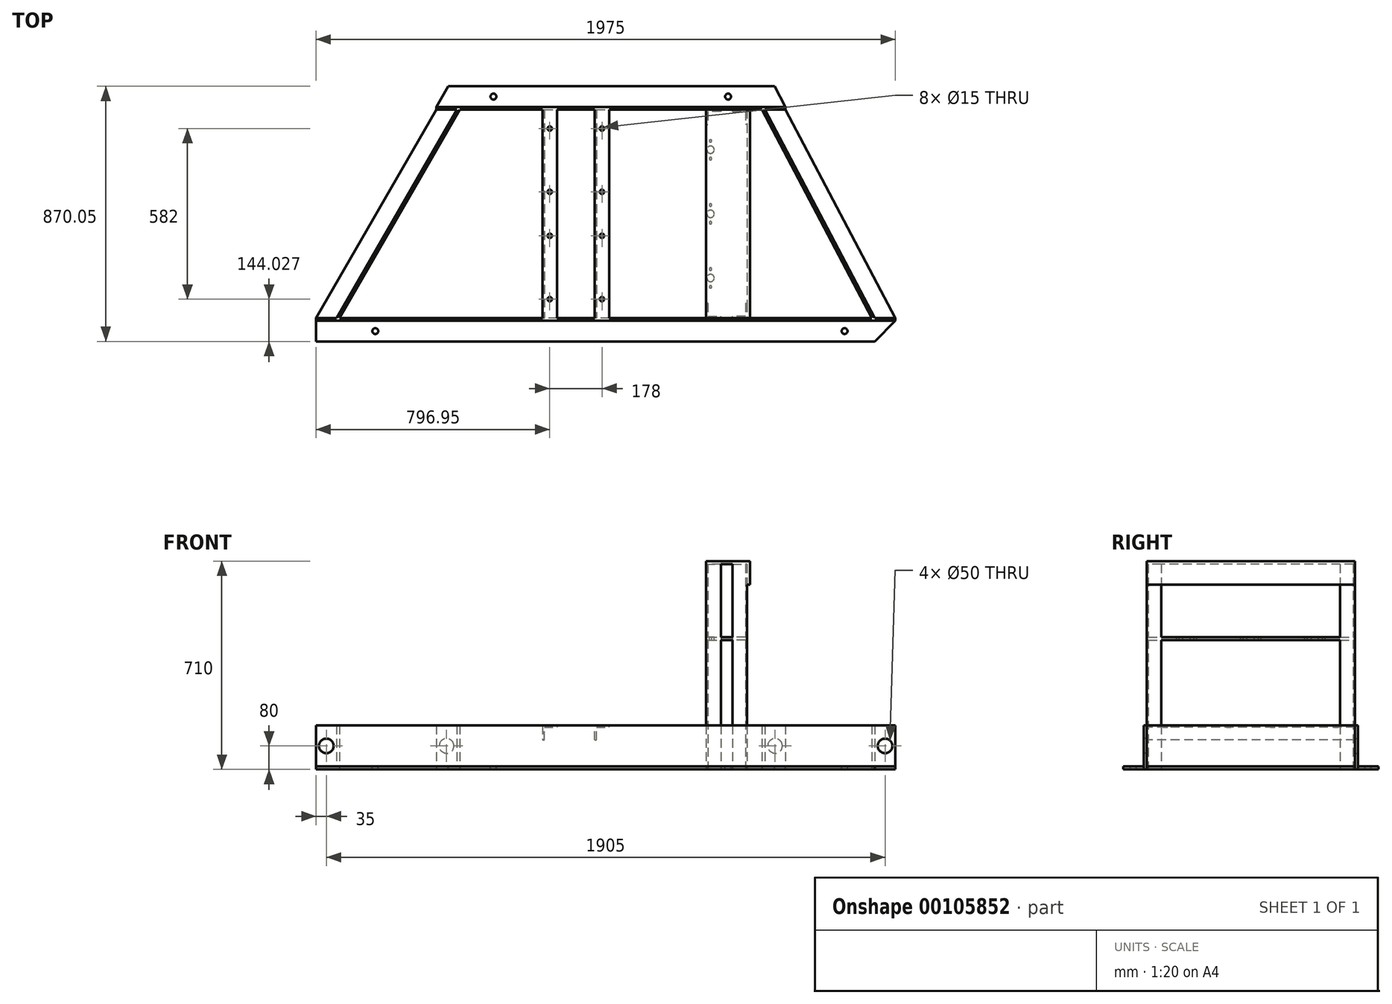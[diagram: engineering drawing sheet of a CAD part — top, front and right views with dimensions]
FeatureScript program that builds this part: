
annotation { "Feature Type Name" : "Feature", "Feature Type Description" : "" }
export const myFeature = defineFeature(function(context is Context, id is Id, definition is map)
    precondition{}
    {
        {
            var Q0;
            Q0=qCreatedBy(makeId("Right.planeOp"),FACE);
            var sketch = newSketch(context, id + "F0", { "sketchPlane" : qUnion([Q0])});
            skLineSegment(sketch, "E0.bottom", {"start": v(0, 0) * mm, "end": v(80, 0) * mm});
            skLineSegment(sketch, "E0.top", {"start": v(0, 10) * mm, "end": v(80, 10) * mm});
            skLineSegment(sketch, "E0.left", {"start": v(0, 0) * mm, "end": v(0, 10) * mm});
            skLineSegment(sketch, "E0.right", {"start": v(80, 0) * mm, "end": v(80, 10) * mm});
            skLineSegment(sketch, "E1.bottom", {"start": v(80, 0) * mm, "end": v(70, 0) * mm});
            skLineSegment(sketch, "E1.top", {"start": v(80, 150) * mm, "end": v(70, 150) * mm});
            skLineSegment(sketch, "E1.left", {"start": v(80, 0) * mm, "end": v(80, 150) * mm});
            skLineSegment(sketch, "E1.right", {"start": v(70, 0) * mm, "end": v(70, 150) * mm});
            skSolve(sketch);
        }
        {
            var Q0;
            Q0 = qSketchRegion(id + "F0", true);
            extrude(context, id + "F1", {"entities" : qUnion([Q0]), "depth" : 1975 * mm});
        }
        {
            var Q0;
            Q0=qCreatedBy(makeId("Top.planeOp"),FACE);
            var sketch = newSketch(context, id + "F2", { "sketchPlane" : qUnion([Q0])});
            skLineSegment(sketch, "E2", {"start": v(0, 80) * mm, "end": v(409.95, 790.05) * mm});
            skLineSegment(sketch, "E3", {"start": v(80, 80) * mm, "end": v(489.95, 790.05) * mm});
            skLineSegment(sketch, "E4", {"start": v(409.95, 790.05) * mm, "end": v(489.95, 790.05) * mm});
            skLineSegment(sketch, "E5", {"start": v(0, 80) * mm, "end": v(80, 80) * mm});
            skSolve(sketch);
        }
        {
            var Q0;
            Q0=makeQuery(id+"F2.imprint","IMPRINT",FACE,{"disambiguationData":[TD([[makeQuery(id+"F2.imprint","IMPRINT",EDGE,{"derivedFrom":sQuery(id+"F2.wireOp",EDGE,"E2")}),-1.0]])]});
            extrude(context, id + "F3", {"entities" : qUnion([Q0]), "operationType" : NewBodyOperationType.ADD, "depth" : 10 * mm});
        }
        {
            var Q0;
            Q0=makeQuery(id+"F3.opExtrude","CAP_FACE",FACE,{"disambiguationData":[OSD([sQuery(id+"F2.wireOp",EDGE,"E2"),sQuery(id+"F2.wireOp",EDGE,"E3"),sQuery(id+"F2.wireOp",EDGE,"E4"),sQuery(id+"F2.wireOp",EDGE,"E5")])],"isStart":false});
            var sketch = newSketch(context, id + "F4", { "sketchPlane" : qUnion([Q0])});
            skLineSegment(sketch, "E6", {"start": v(489.95, 790.05) * mm, "end": v(80, 80) * mm});
            skLineSegment(sketch, "E7", {"start": v(80, 80) * mm, "end": v(70, 80) * mm});
            skLineSegment(sketch, "E8", {"start": v(70, 80) * mm, "end": v(479.95, 790.05) * mm});
            skLineSegment(sketch, "E9", {"start": v(479.95, 790.05) * mm, "end": v(489.95, 790.05) * mm});
            skSolve(sketch);
        }
        {
            var Q0;
            Q0 = qSketchRegion(id + "F4", true);
            extrude(context, id + "F5", {"entities" : qUnion([Q0]), "operationType" : NewBodyOperationType.ADD, "depth" : 140 * mm});
        }
        {
            var Q0;
            Q0=qCreatedBy(makeId("Top.planeOp"),FACE);
            var sketch = newSketch(context, id + "F6", { "sketchPlane" : qUnion([Q0])});
            skLineSegment(sketch, "E10", {"start": v(409.95, 790.05) * mm, "end": v(1599.95, 790.05) * mm});
            skLineSegment(sketch, "E11", {"start": v(409.95, 790.05) * mm, "end": v(409.95, 870.05) * mm});
            skLineSegment(sketch, "E12", {"start": v(409.95, 870.05) * mm, "end": v(1599.95, 870.05) * mm});
            skLineSegment(sketch, "E13", {"start": v(1599.95, 870.05) * mm, "end": v(1599.95, 790.05) * mm});
            skSolve(sketch);
        }
        {
            var Q0;
            Q0 = qSketchRegion(id + "F6", true);
            extrude(context, id + "F7", {"entities" : qUnion([Q0]), "operationType" : NewBodyOperationType.ADD, "depth" : 10 * mm});
        }
        {
            var Q0;
            Q0=makeQuery(id+"F7.boolean.opBoolean","MERGE",FACE,{"derivedFrom":[makeQuery(id+"F3.opExtrude","CAP_FACE",FACE,{"disambiguationData":[OSD([sQuery(id+"F2.wireOp",EDGE,"E2"),sQuery(id+"F2.wireOp",EDGE,"E3"),sQuery(id+"F2.wireOp",EDGE,"E4"),sQuery(id+"F2.wireOp",EDGE,"E5")])],"isStart":false}),makeQuery(id+"F7.opExtrude","CAP_FACE",FACE,{"disambiguationData":[OSD([sQuery(id+"F6.wireOp",EDGE,"E10"),sQuery(id+"F6.wireOp",EDGE,"E11"),sQuery(id+"F6.wireOp",EDGE,"E12"),sQuery(id+"F6.wireOp",EDGE,"E13")])],"isStart":false})]});
            var sketch = newSketch(context, id + "F8", { "sketchPlane" : qUnion([Q0])});
            skLineSegment(sketch, "E14", {"start": v(409.95, 790.05) * mm, "end": v(1599.95, 790.05) * mm});
            skLineSegment(sketch, "E15", {"start": v(1599.95, 790.05) * mm, "end": v(1599.95, 800.05) * mm});
            skLineSegment(sketch, "E16", {"start": v(1599.95, 800.05) * mm, "end": v(409.95, 800.05) * mm});
            skLineSegment(sketch, "E17", {"start": v(409.95, 800.05) * mm, "end": v(409.95, 790.05) * mm});
            skSolve(sketch);
        }
        {
            var Q0;
            Q0 = qSketchRegion(id + "F8", true);
            extrude(context, id + "F9", {"entities" : qUnion([Q0]), "operationType" : NewBodyOperationType.ADD, "depth" : 140 * mm});
        }
        {
            var Q0;
            Q0=qCreatedBy(makeId("Top.planeOp"),FACE);
            var sketch = newSketch(context, id + "F10", { "sketchPlane" : qUnion([Q0])});
            skLineSegment(sketch, "E18", {"start": v(1599.95, 790.05) * mm, "end": v(1975, 80) * mm});
            skLineSegment(sketch, "E19", {"start": v(1975, 80) * mm, "end": v(1895, 80) * mm});
            skLineSegment(sketch, "E20", {"start": v(1895, 80) * mm, "end": v(1519.95, 790.05) * mm});
            skLineSegment(sketch, "E21", {"start": v(1519.95, 790.05) * mm, "end": v(1599.95, 790.05) * mm});
            skSolve(sketch);
        }
        {
            var Q0;
            Q0 = qSketchRegion(id + "F10", true);
            extrude(context, id + "F11", {"entities" : qUnion([Q0]), "operationType" : NewBodyOperationType.ADD, "depth" : 10 * mm});
        }
        {
            var Q0;
            Q0=makeQuery(id+"F11.opExtrude","CAP_FACE",FACE,{"disambiguationData":[OSD([sQuery(id+"F10.wireOp",EDGE,"E18"),sQuery(id+"F10.wireOp",EDGE,"E19"),sQuery(id+"F10.wireOp",EDGE,"E20"),sQuery(id+"F10.wireOp",EDGE,"E21")])],"isStart":false});
            var sketch = newSketch(context, id + "F12", { "sketchPlane" : qUnion([Q0])});
            skLineSegment(sketch, "E22", {"start": v(1519.95, 790.05) * mm, "end": v(1895, 80) * mm});
            skLineSegment(sketch, "E23", {"start": v(1895, 80) * mm, "end": v(1905, 80) * mm});
            skLineSegment(sketch, "E24", {"start": v(1905, 80) * mm, "end": v(1529.95, 790.05) * mm});
            skLineSegment(sketch, "E25", {"start": v(1529.95, 790.05) * mm, "end": v(1519.95, 790.05) * mm});
            skSolve(sketch);
        }
        {
            var Q0;
            Q0 = qSketchRegion(id + "F12", true);
            extrude(context, id + "F13", {"entities" : qUnion([Q0]), "operationType" : NewBodyOperationType.ADD, "depth" : 140 * mm});
        }
        {
            var Q0;
            Q0=makeQuery(id+"F1.opExtrude","SWEPT_FACE",FACE,{"disambiguationData":[OSD([sQuery(id+"F0.wireOp",EDGE,"E1.right")])]});
            var sketch = newSketch(context, id + "F14", { "sketchPlane" : qUnion([Q0])});
            skPoint(sketch, "E26", {"position": v(35, 80) * mm});
            skPoint(sketch, "E27", {"position": v(1940, 80) * mm});
            skSolve(sketch);
        }
        {
            var Q0;
            Q0=sQuery(id+"F14.wireOp",VERTEX,"E26");
            var Q1;
            Q1=sQuery(id+"F14.wireOp",VERTEX,"E27");
            var Q2;
            Q2=makeQuery(id+"F1.opExtrude","SWEPT_BODY",BODY,{"disambiguationData":[OSD([sQuery(id+"F0.wireOp",EDGE,"E0.bottom"),sQuery(id+"F0.wireOp",EDGE,"E0.top"),sQuery(id+"F0.wireOp",EDGE,"E0.left"),sQuery(id+"F0.wireOp",EDGE,"E1.bottom"),sQuery(id+"F0.wireOp",EDGE,"E1.top"),sQuery(id+"F0.wireOp",EDGE,"E1.left"),sQuery(id+"F0.wireOp",EDGE,"E1.right")])]});
            hole(context, id + "F15", {"style" : HoleStyle.SIMPLE, "endStyle" : HoleEndStyle.THROUGH, "holeDiameter" : 50 * mm, "locations" : qUnion([Q0, Q1]), "scope" : qUnion([Q2]), "isTappedThrough" : true});
        }
        {
            var Q0;
            Q0=makeQuery(id+"F9.opExtrude","SWEPT_FACE",FACE,{"disambiguationData":[OSD([sQuery(id+"F8.wireOp",EDGE,"E16")])]});
            var sketch = newSketch(context, id + "F16", { "sketchPlane" : qUnion([Q0])});
            skPoint(sketch, "E28", {"position": v(-1564.95, 80) * mm});
            skPoint(sketch, "E29", {"position": v(-444.95, 80) * mm});
            skSolve(sketch);
        }
        {
            var Q0;
            Q0=sQuery(id+"F16.wireOp",VERTEX,"E28");
            var Q1;
            Q1=sQuery(id+"F16.wireOp",VERTEX,"E29");
            var Q2;
            Q2=makeQuery(id+"F1.opExtrude","SWEPT_BODY",BODY,{"disambiguationData":[OSD([sQuery(id+"F0.wireOp",EDGE,"E0.bottom"),sQuery(id+"F0.wireOp",EDGE,"E0.top"),sQuery(id+"F0.wireOp",EDGE,"E0.left"),sQuery(id+"F0.wireOp",EDGE,"E1.bottom"),sQuery(id+"F0.wireOp",EDGE,"E1.top"),sQuery(id+"F0.wireOp",EDGE,"E1.left"),sQuery(id+"F0.wireOp",EDGE,"E1.right")])]});
            hole(context, id + "F17", {"style" : HoleStyle.SIMPLE, "endStyle" : HoleEndStyle.BLIND, "holeDiameter" : 50 * mm, "holeDepth" : 12 * mm, "locations" : qUnion([Q0, Q1]), "scope" : qUnion([Q2])});
        }
        {
            var Q0;
            Q0=makeQuery(id+"F13.boolean.opBoolean","MERGE",FACE,{"derivedFrom":[makeQuery(id+"F9.boolean.opBoolean","MERGE",FACE,{"derivedFrom":[makeQuery(id+"F5.boolean.opBoolean","MERGE",FACE,{"derivedFrom":[makeQuery(id+"F1.opExtrude","SWEPT_FACE",FACE,{"disambiguationData":[OSD([sQuery(id+"F0.wireOp",EDGE,"E1.top")])]}),makeQuery(id+"F5.opExtrude","CAP_FACE",FACE,{"disambiguationData":[OSD([sQuery(id+"F4.wireOp",EDGE,"E6"),sQuery(id+"F4.wireOp",EDGE,"E7"),sQuery(id+"F4.wireOp",EDGE,"E8"),sQuery(id+"F4.wireOp",EDGE,"E9")])],"isStart":false})]}),makeQuery(id+"F9.opExtrude","CAP_FACE",FACE,{"disambiguationData":[OSD([sQuery(id+"F8.wireOp",EDGE,"E14"),sQuery(id+"F8.wireOp",EDGE,"E15"),sQuery(id+"F8.wireOp",EDGE,"E16"),sQuery(id+"F8.wireOp",EDGE,"E17")])],"isStart":false})]}),makeQuery(id+"F13.opExtrude","CAP_FACE",FACE,{"disambiguationData":[OSD([sQuery(id+"F12.wireOp",EDGE,"E22"),sQuery(id+"F12.wireOp",EDGE,"E23"),sQuery(id+"F12.wireOp",EDGE,"E24"),sQuery(id+"F12.wireOp",EDGE,"E25")])],"isStart":false})]});
            var sketch = newSketch(context, id + "F18", { "sketchPlane" : qUnion([Q0])});
            skLineSegment(sketch, "E30.bottom", {"start": v(771.95, 70) * mm, "end": v(821.95, 70) * mm});
            skLineSegment(sketch, "E30.top", {"start": v(771.95, 800.05) * mm, "end": v(821.95, 800.05) * mm});
            skLineSegment(sketch, "E30.left", {"start": v(771.95, 70) * mm, "end": v(771.95, 800.05) * mm});
            skLineSegment(sketch, "E30.right", {"start": v(821.95, 70) * mm, "end": v(821.95, 800.05) * mm});
            skLineSegment(sketch, "E31.bottom", {"start": v(949.95, 800.05) * mm, "end": v(999.95, 800.05) * mm});
            skLineSegment(sketch, "E31.top", {"start": v(949.95, 70) * mm, "end": v(999.95, 70) * mm});
            skLineSegment(sketch, "E31.left", {"start": v(999.95, 800.05) * mm, "end": v(999.95, 70) * mm});
            skLineSegment(sketch, "E31.right", {"start": v(949.95, 800.05) * mm, "end": v(949.95, 70) * mm});
            skLineSegment(sketch, "E32", {"start": v(771.95, 435.03) * mm, "end": v(1167.6, 435.03) * mm, "construction": true});
            skPoint(sketch, "E32.endSnap0", {"position": v(771.95, 435.03) * mm});
            skCircle(sketch, "E33", {"center": v(796.95, 144.03) * mm, "radius": 7.5 * mm});
            skPoint(sketch, "E33.centerSnap0", {"position": v(796.95, 70) * mm});
            skCircle(sketch, "E34", {"center": v(796.95, 360.03) * mm, "radius": 7.5 * mm});
            skCircle(sketch, "E35.1.0.0", {"center": v(974.95, 144.03) * mm, "radius": 7.5 * mm});
            skCircle(sketch, "E35.1.0.1", {"center": v(974.95, 360.03) * mm, "radius": 7.5 * mm});
            skLineSegment(sketch, "E35.direction1", {"start": v(796.95, 144.03) * mm, "end": v(974.95, 144.03) * mm, "construction": true});
            skCircle(sketch, "E36.MirrorC", {"center": v(796.95, 510.03) * mm, "radius": 7.5 * mm});
            skCircle(sketch, "E37.MirrorC", {"center": v(796.95, 726.03) * mm, "radius": 7.5 * mm});
            skCircle(sketch, "E38.MirrorC", {"center": v(974.95, 510.03) * mm, "radius": 7.5 * mm});
            skCircle(sketch, "E39.MirrorC", {"center": v(974.95, 726.03) * mm, "radius": 7.5 * mm});
            skSolve(sketch);
        }
        {
            var Q0;
            Q0 = qSketchRegion(id + "F18", true);
            extrude(context, id + "F19", {"entities" : qUnion([Q0]), "operationType" : NewBodyOperationType.ADD, "oppositeDirection" : true, "depth" : 6 * mm});
        }
        {
            var Q0;
            Q0=makeQuery(id+"F19.opExtrude","CAP_FACE",FACE,{"disambiguationData":[OSD([sQuery(id+"F18.wireOp",EDGE,"E31.bottom"),sQuery(id+"F18.wireOp",EDGE,"E31.top"),sQuery(id+"F18.wireOp",EDGE,"E31.left"),sQuery(id+"F18.wireOp",EDGE,"E31.right"),sQuery(id+"F18.wireOp",EDGE,"E35.1.0.0"),sQuery(id+"F18.wireOp",EDGE,"E35.1.0.1"),sQuery(id+"F18.wireOp",EDGE,"E38.MirrorC"),sQuery(id+"F18.wireOp",EDGE,"E39.MirrorC")])],"isStart":false});
            var sketch = newSketch(context, id + "F20", { "sketchPlane" : qUnion([Q0])});
            skLineSegment(sketch, "E40.bottom", {"start": v(949.95, -790.05) * mm, "end": v(955.95, -790.05) * mm});
            skLineSegment(sketch, "E40.top", {"start": v(949.95, -80) * mm, "end": v(955.95, -80) * mm});
            skLineSegment(sketch, "E40.left", {"start": v(949.95, -790.05) * mm, "end": v(949.95, -80) * mm});
            skLineSegment(sketch, "E40.right", {"start": v(955.95, -790.05) * mm, "end": v(955.95, -80) * mm});
            skLineSegment(sketch, "E41.1.0.0", {"start": v(771.95, -790.05) * mm, "end": v(771.95, -80) * mm});
            skLineSegment(sketch, "E41.1.0.1", {"start": v(777.95, -790.05) * mm, "end": v(777.95, -80) * mm});
            skLineSegment(sketch, "E41.1.0.2", {"start": v(771.95, -790.05) * mm, "end": v(777.95, -790.05) * mm});
            skLineSegment(sketch, "E41.1.0.3", {"start": v(771.95, -80) * mm, "end": v(777.95, -80) * mm});
            skLineSegment(sketch, "E41.direction1", {"start": v(949.95, -790.05) * mm, "end": v(771.95, -790.05) * mm, "construction": true});
            skSolve(sketch);
        }
        {
            var Q0;
            Q0 = qSketchRegion(id + "F20", true);
            extrude(context, id + "F21", {"entities" : qUnion([Q0]), "operationType" : NewBodyOperationType.ADD, "depth" : 44 * mm});
        }
        {
            var Q0;
            Q0=qCreatedBy(makeId("Top.planeOp"),FACE);
            var sketch = newSketch(context, id + "F22", { "sketchPlane" : qUnion([Q0])});
            skLineSegment(sketch, "E42.bottom", {"start": v(1419.95, 790.05) * mm, "end": v(1469.95, 790.05) * mm});
            skLineSegment(sketch, "E42.top", {"start": v(1419.95, 784.05) * mm, "end": v(1469.95, 784.05) * mm});
            skLineSegment(sketch, "E42.left", {"start": v(1419.95, 790.05) * mm, "end": v(1419.95, 784.05) * mm});
            skLineSegment(sketch, "E42.right", {"start": v(1469.95, 790.05) * mm, "end": v(1469.95, 784.05) * mm});
            skLineSegment(sketch, "E43.bottom", {"start": v(1469.95, 790.05) * mm, "end": v(1463.95, 790.05) * mm});
            skLineSegment(sketch, "E43.top", {"start": v(1469.95, 740.05) * mm, "end": v(1463.95, 740.05) * mm});
            skLineSegment(sketch, "E43.left", {"start": v(1469.95, 790.05) * mm, "end": v(1469.95, 740.05) * mm});
            skLineSegment(sketch, "E43.right", {"start": v(1463.95, 790.05) * mm, "end": v(1463.95, 740.05) * mm});
            skLineSegment(sketch, "E44.bottom", {"start": v(1463.95, 130) * mm, "end": v(1469.95, 130) * mm});
            skLineSegment(sketch, "E44.top", {"start": v(1463.95, 80) * mm, "end": v(1469.95, 80) * mm});
            skLineSegment(sketch, "E44.left", {"start": v(1463.95, 130) * mm, "end": v(1463.95, 80) * mm});
            skLineSegment(sketch, "E44.right", {"start": v(1469.95, 130) * mm, "end": v(1469.95, 80) * mm});
            skLineSegment(sketch, "E45.bottom", {"start": v(1463.95, 80) * mm, "end": v(1419.95, 80) * mm});
            skLineSegment(sketch, "E45.top", {"start": v(1463.95, 86) * mm, "end": v(1419.95, 86) * mm});
            skLineSegment(sketch, "E45.left", {"start": v(1463.95, 80) * mm, "end": v(1463.95, 86) * mm});
            skLineSegment(sketch, "E45.right", {"start": v(1419.95, 80) * mm, "end": v(1419.95, 86) * mm});
            skLineSegment(sketch, "E46", {"start": v(1399.95, 829.97) * mm, "end": v(1399.95, -33.08) * mm, "construction": true});
            skLineSegment(sketch, "E47.MirrorCS", {"start": v(1329.95, 790.05) * mm, "end": v(1329.95, 740.05) * mm});
            skLineSegment(sketch, "E48.MirrorCS", {"start": v(1335.95, 790.05) * mm, "end": v(1335.95, 740.05) * mm});
            skLineSegment(sketch, "E49.MirrorCS", {"start": v(1379.95, 784.05) * mm, "end": v(1329.95, 784.05) * mm});
            skLineSegment(sketch, "E50.MirrorCS", {"start": v(1379.95, 790.05) * mm, "end": v(1329.95, 790.05) * mm});
            skLineSegment(sketch, "E51.MirrorCS", {"start": v(1329.95, 740.05) * mm, "end": v(1335.95, 740.05) * mm});
            skLineSegment(sketch, "E52.MirrorCS", {"start": v(1379.95, 790.05) * mm, "end": v(1379.95, 784.05) * mm});
            skLineSegment(sketch, "E53.MirrorCS", {"start": v(1329.95, 130) * mm, "end": v(1329.95, 80) * mm});
            skLineSegment(sketch, "E54.MirrorCS", {"start": v(1335.95, 130) * mm, "end": v(1329.95, 130) * mm});
            skLineSegment(sketch, "E55.MirrorCS", {"start": v(1335.95, 86) * mm, "end": v(1379.95, 86) * mm});
            skLineSegment(sketch, "E56.MirrorCS", {"start": v(1335.95, 80) * mm, "end": v(1379.95, 80) * mm});
            skLineSegment(sketch, "E57.MirrorCS", {"start": v(1379.95, 80) * mm, "end": v(1379.95, 86) * mm});
            skPoint(sketch, "E58.orphan", {"position": v(1335.95, 80) * mm});
            skPoint(sketch, "E59.MirrorCS.start.orphan", {"position": v(1335.95, 130) * mm});
            skLineSegment(sketch, "E60", {"start": v(1335.95, 130) * mm, "end": v(1335.95, 86) * mm});
            skLineSegment(sketch, "E61", {"start": v(1329.95, 80) * mm, "end": v(1335.95, 80) * mm});
            skSolve(sketch);
        }
        {
            var Q0;
            Q0 = qSketchRegion(id + "F22", true);
            extrude(context, id + "F23", {"entities" : qUnion([Q0]), "operationType" : NewBodyOperationType.ADD, "depth" : 700 * mm});
        }
        {
            var Q0;
            Q0=makeQuery(id+"F23.opExtrude","CAP_FACE",FACE,{"disambiguationData":[OSD([sQuery(id+"F22.wireOp",EDGE,"E44.bottom"),sQuery(id+"F22.wireOp",EDGE,"E44.top"),sQuery(id+"F22.wireOp",EDGE,"E44.left"),sQuery(id+"F22.wireOp",EDGE,"E44.right"),sQuery(id+"F22.wireOp",EDGE,"E45.bottom"),sQuery(id+"F22.wireOp",EDGE,"E45.top"),sQuery(id+"F22.wireOp",EDGE,"E45.right")])],"isStart":false});
            var sketch = newSketch(context, id + "F24", { "sketchPlane" : qUnion([Q0])});
            skLineSegment(sketch, "E62.bottom", {"start": v(1329.95, 790) * mm, "end": v(1479.95, 790) * mm});
            skLineSegment(sketch, "E62.top", {"start": v(1329.95, 80) * mm, "end": v(1479.95, 80) * mm});
            skLineSegment(sketch, "E62.left", {"start": v(1329.95, 790) * mm, "end": v(1329.95, 80) * mm});
            skLineSegment(sketch, "E62.right", {"start": v(1479.95, 790) * mm, "end": v(1479.95, 80) * mm});
            skSolve(sketch);
        }
        {
            var Q0;
            Q0 = qSketchRegion(id + "F24", true);
            extrude(context, id + "F25", {"entities" : qUnion([Q0]), "operationType" : NewBodyOperationType.ADD, "depth" : 10 * mm});
        }
        {
            var Q0;
            Q0=makeQuery(id+"F25.opExtrude","CAP_FACE",FACE,{"disambiguationData":[OSD([sQuery(id+"F24.wireOp",EDGE,"E62.bottom"),sQuery(id+"F24.wireOp",EDGE,"E62.top"),sQuery(id+"F24.wireOp",EDGE,"E62.left"),sQuery(id+"F24.wireOp",EDGE,"E62.right")])],"isStart":true});
            var sketch = newSketch(context, id + "F26", { "sketchPlane" : qUnion([Q0])});
            skLineSegment(sketch, "E63.bottom", {"start": v(1479.95, -80) * mm, "end": v(1469.95, -80) * mm});
            skLineSegment(sketch, "E63.top", {"start": v(1479.95, -790) * mm, "end": v(1469.95, -790) * mm});
            skLineSegment(sketch, "E63.left", {"start": v(1479.95, -80) * mm, "end": v(1479.95, -790) * mm});
            skLineSegment(sketch, "E63.right", {"start": v(1469.95, -80) * mm, "end": v(1469.95, -790) * mm});
            skSolve(sketch);
        }
        {
            var Q0;
            Q0 = qSketchRegion(id + "F26", true);
            extrude(context, id + "F27", {"entities" : qUnion([Q0]), "operationType" : NewBodyOperationType.ADD, "depth" : 70 * mm});
        }
        {
            var Q0;
            Q0=makeQuery(id+"F27.boolean.opBoolean","MERGE",FACE,{"derivedFrom":[makeQuery(id+"F25.boolean.opBoolean","MERGE",FACE,{"derivedFrom":[makeQuery(id+"F23.opExtrude","SWEPT_FACE",FACE,{"disambiguationData":[OSD([sQuery(id+"F22.wireOp",EDGE,"E44.top"),sQuery(id+"F22.wireOp",EDGE,"E45.bottom")])]}),makeQuery(id+"F23.opExtrude","SWEPT_FACE",FACE,{"disambiguationData":[OSD([sQuery(id+"F22.wireOp",EDGE,"E56.MirrorCS"),sQuery(id+"F22.wireOp",EDGE,"E61")])]}),makeQuery(id+"F25.opExtrude","SWEPT_FACE",FACE,{"disambiguationData":[OSD([sQuery(id+"F24.wireOp",EDGE,"E62.top")])]})]}),makeQuery(id+"F27.opExtrude","SWEPT_FACE",FACE,{"disambiguationData":[OSD([sQuery(id+"F26.wireOp",EDGE,"E63.bottom")])]})]});
            var sketch = newSketch(context, id + "F28", { "sketchPlane" : qUnion([Q0])});
            skLineSegment(sketch, "E64.bottom", {"start": v(1329.95, 451.5) * mm, "end": v(1469.95, 451.5) * mm});
            skLineSegment(sketch, "E64.top", {"start": v(1329.95, 441.5) * mm, "end": v(1469.95, 441.5) * mm});
            skLineSegment(sketch, "E64.left", {"start": v(1329.95, 451.5) * mm, "end": v(1329.95, 441.5) * mm});
            skLineSegment(sketch, "E64.right", {"start": v(1469.95, 451.5) * mm, "end": v(1469.95, 441.5) * mm});
            skSolve(sketch);
        }
        {
            var Q0;
            Q0 = qSketchRegion(id + "F28", true);
            extrude(context, id + "F29", {"entities" : qUnion([Q0]), "operationType" : NewBodyOperationType.ADD, "oppositeDirection" : true, "depth" : 710 * mm});
        }
        {
            var Q0;
            Q0=makeQuery(id+"F29.opExtrude","SWEPT_FACE",FACE,{"disambiguationData":[OSD([sQuery(id+"F28.wireOp",EDGE,"E64.bottom")])]});
            var sketch = newSketch(context, id + "F30", { "sketchPlane" : qUnion([Q0])});
            skPoint(sketch, "E65", {"position": v(1430.8, 487) * mm});
            skPoint(sketch, "E66", {"position": v(1376.8, 487) * mm});
            skPoint(sketch, "E67", {"position": v(1430.8, 383) * mm});
            skPoint(sketch, "E68", {"position": v(1376.8, 383) * mm});
            skPoint(sketch, "E69", {"position": v(1344.95, 684.05) * mm});
            skPoint(sketch, "E70", {"position": v(1344.95, 623.45) * mm});
            skPoint(sketch, "E71", {"position": v(1344.95, 246.6) * mm});
            skPoint(sketch, "E72", {"position": v(1344.95, 186) * mm});
            skCircle(sketch, "E73", {"center": v(1344.95, 216.3) * mm, "radius": 12.5 * mm});
            skCircle(sketch, "E74", {"center": v(1344.95, 653.75) * mm, "radius": 12.5 * mm});
            skPoint(sketch, "E75", {"position": v(1344.95, 404.7) * mm});
            skPoint(sketch, "E76", {"position": v(1344.95, 465.3) * mm});
            skCircle(sketch, "E77", {"center": v(1344.95, 435) * mm, "radius": 12.5 * mm});
            skSolve(sketch);
        }
        {
            var Q0;
            Q0=sQuery(id+"F30.wireOp",VERTEX,"E70");
            var Q1;
            Q1=sQuery(id+"F30.wireOp",VERTEX,"E69");
            var Q2;
            Q2=sQuery(id+"F30.wireOp",VERTEX,"E71");
            var Q3;
            Q3=sQuery(id+"F30.wireOp",VERTEX,"E72");
            var Q4;
            Q4=sQuery(id+"F30.wireOp",VERTEX,"E75");
            var Q5;
            Q5=sQuery(id+"F30.wireOp",VERTEX,"E76");
            var Q6;
            Q6=makeQuery(id+"F1.opExtrude","SWEPT_BODY",BODY,{"disambiguationData":[OSD([sQuery(id+"F0.wireOp",EDGE,"E0.bottom"),sQuery(id+"F0.wireOp",EDGE,"E0.top"),sQuery(id+"F0.wireOp",EDGE,"E0.left"),sQuery(id+"F0.wireOp",EDGE,"E1.bottom"),sQuery(id+"F0.wireOp",EDGE,"E1.top"),sQuery(id+"F0.wireOp",EDGE,"E1.left"),sQuery(id+"F0.wireOp",EDGE,"E1.right")])]});
            hole(context, id + "F31", {"style" : HoleStyle.SIMPLE, "endStyle" : HoleEndStyle.BLIND, "standardTappedOrClearance" : lookupTablePath({ "standard" : "ISO", "fit" : "Normal", "size" : "M8", "type" : "Clearance" }), "standardBlindInLast" : lookupTablePath({ "fit" : "Standard", "standard" : "ISO", "size" : "M8", "type" : "Clearance" }), "holeDiameter" : 8.8 * mm, "holeDepth" : 20 * mm, "locations" : qUnion([Q0, Q1, Q2, Q3, Q4, Q5]), "scope" : qUnion([Q6])});
        }
        {
            var Q0;
            Q0 = qSketchRegion(id + "F30", true);
            extrude(context, id + "F32", {"entities" : qUnion([Q0]), "operationType" : NewBodyOperationType.REMOVE, "oppositeDirection" : true, "depth" : 25 * mm});
        }
        {
            var Q0;
            {var subQ0=sQuery(id+"F6.wireOp",EDGE,"E13");var subQ1=sQuery(id+"F6.wireOp",EDGE,"E12");var subQ2=sQuery(id+"F6.wireOp",EDGE,"E11");Q0=makeQuery(id+"F9.boolean.opBoolean","SPLIT",FACE,{"disambiguationData":[TD([makeQuery(id+"F7.opExtrude","SWEPT_FACE",FACE,{"disambiguationData":[OSD([subQ1])]})])],"derivedFrom":makeQuery(id+"F7.boolean.opBoolean","MERGE",FACE,{"derivedFrom":[makeQuery(id+"F3.opExtrude","CAP_FACE",FACE,{"disambiguationData":[OSD([sQuery(id+"F2.wireOp",EDGE,"E2"),sQuery(id+"F2.wireOp",EDGE,"E3"),sQuery(id+"F2.wireOp",EDGE,"E4"),sQuery(id+"F2.wireOp",EDGE,"E5")])],"isStart":false}),makeQuery(id+"F7.opExtrude","CAP_FACE",FACE,{"disambiguationData":[OSD([sQuery(id+"F6.wireOp",EDGE,"E10"),subQ2,subQ1,subQ0])],"isStart":false})]})});}
            var sketch = newSketch(context, id + "F33", { "sketchPlane" : qUnion([Q0])});
            skPoint(sketch, "E78", {"position": v(604.95, 835.05) * mm});
            skPoint(sketch, "E79", {"position": v(1404.95, 835.05) * mm});
            skPoint(sketch, "E80", {"position": v(1802, 35) * mm});
            skPoint(sketch, "E81", {"position": v(202, 35) * mm});
            skSolve(sketch);
        }
        {
            var Q0;
            Q0=sQuery(id+"F33.wireOp",VERTEX,"E81");
            var Q1;
            Q1=sQuery(id+"F33.wireOp",VERTEX,"E80");
            var Q2;
            Q2=sQuery(id+"F33.wireOp",VERTEX,"E79");
            var Q3;
            Q3=sQuery(id+"F33.wireOp",VERTEX,"E78");
            var Q4;
            Q4=makeQuery(id+"F1.opExtrude","SWEPT_BODY",BODY,{"disambiguationData":[OSD([sQuery(id+"F0.wireOp",EDGE,"E0.bottom"),sQuery(id+"F0.wireOp",EDGE,"E0.top"),sQuery(id+"F0.wireOp",EDGE,"E0.left"),sQuery(id+"F0.wireOp",EDGE,"E1.bottom"),sQuery(id+"F0.wireOp",EDGE,"E1.top"),sQuery(id+"F0.wireOp",EDGE,"E1.left"),sQuery(id+"F0.wireOp",EDGE,"E1.right")])]});
            hole(context, id + "F34", {"style" : HoleStyle.SIMPLE, "endStyle" : HoleEndStyle.THROUGH, "holeDiameter" : 20 * mm, "locations" : qUnion([Q0, Q1, Q2, Q3]), "scope" : qUnion([Q4]), "isTappedThrough" : true});
        }
        {
            var Q0;
            {var subQ0=sQuery(id+"F6.wireOp",EDGE,"E13");var subQ1=sQuery(id+"F6.wireOp",EDGE,"E12");var subQ2=sQuery(id+"F6.wireOp",EDGE,"E11");Q0=makeQuery(id+"F9.boolean.opBoolean","SPLIT",FACE,{"disambiguationData":[TD([makeQuery(id+"F7.opExtrude","SWEPT_FACE",FACE,{"disambiguationData":[OSD([subQ1])]})])],"derivedFrom":makeQuery(id+"F7.boolean.opBoolean","MERGE",FACE,{"derivedFrom":[makeQuery(id+"F3.opExtrude","CAP_FACE",FACE,{"disambiguationData":[OSD([sQuery(id+"F2.wireOp",EDGE,"E2"),sQuery(id+"F2.wireOp",EDGE,"E3"),sQuery(id+"F2.wireOp",EDGE,"E4"),sQuery(id+"F2.wireOp",EDGE,"E5")])],"isStart":false}),makeQuery(id+"F7.opExtrude","CAP_FACE",FACE,{"disambiguationData":[OSD([sQuery(id+"F6.wireOp",EDGE,"E10"),subQ2,subQ1,subQ0])],"isStart":false})]})});}
            var sketch = newSketch(context, id + "F35", { "sketchPlane" : qUnion([Q0])});
            skLineSegment(sketch, "E82", {"start": v(409.95, 800.05) * mm, "end": v(450.36, 870.05) * mm});
            skLineSegment(sketch, "E83", {"start": v(450.36, 870.05) * mm, "end": v(409.95, 870.05) * mm});
            skLineSegment(sketch, "E84", {"start": v(409.95, 870.05) * mm, "end": v(409.95, 800.05) * mm});
            skLineSegment(sketch, "E85", {"start": v(1599.95, 800.05) * mm, "end": v(1562.98, 870.05) * mm});
            skLineSegment(sketch, "E86", {"start": v(1562.98, 870.05) * mm, "end": v(1599.95, 870.05) * mm});
            skLineSegment(sketch, "E87", {"start": v(1599.95, 870.05) * mm, "end": v(1599.95, 800.05) * mm});
            skLineSegment(sketch, "E88", {"start": v(1905, 0) * mm, "end": v(1975, 70) * mm});
            skLineSegment(sketch, "E89", {"start": v(1975, 70) * mm, "end": v(1975, 0) * mm});
            skLineSegment(sketch, "E90", {"start": v(1975, 0) * mm, "end": v(1905, 0) * mm});
            skSolve(sketch);
        }
        {
            var Q0;
            Q0 = qSketchRegion(id + "F35", true);
            extrude(context, id + "F36", {"entities" : qUnion([Q0]), "operationType" : NewBodyOperationType.REMOVE, "oppositeDirection" : true, "depth" : 25 * mm});
        }
    });
